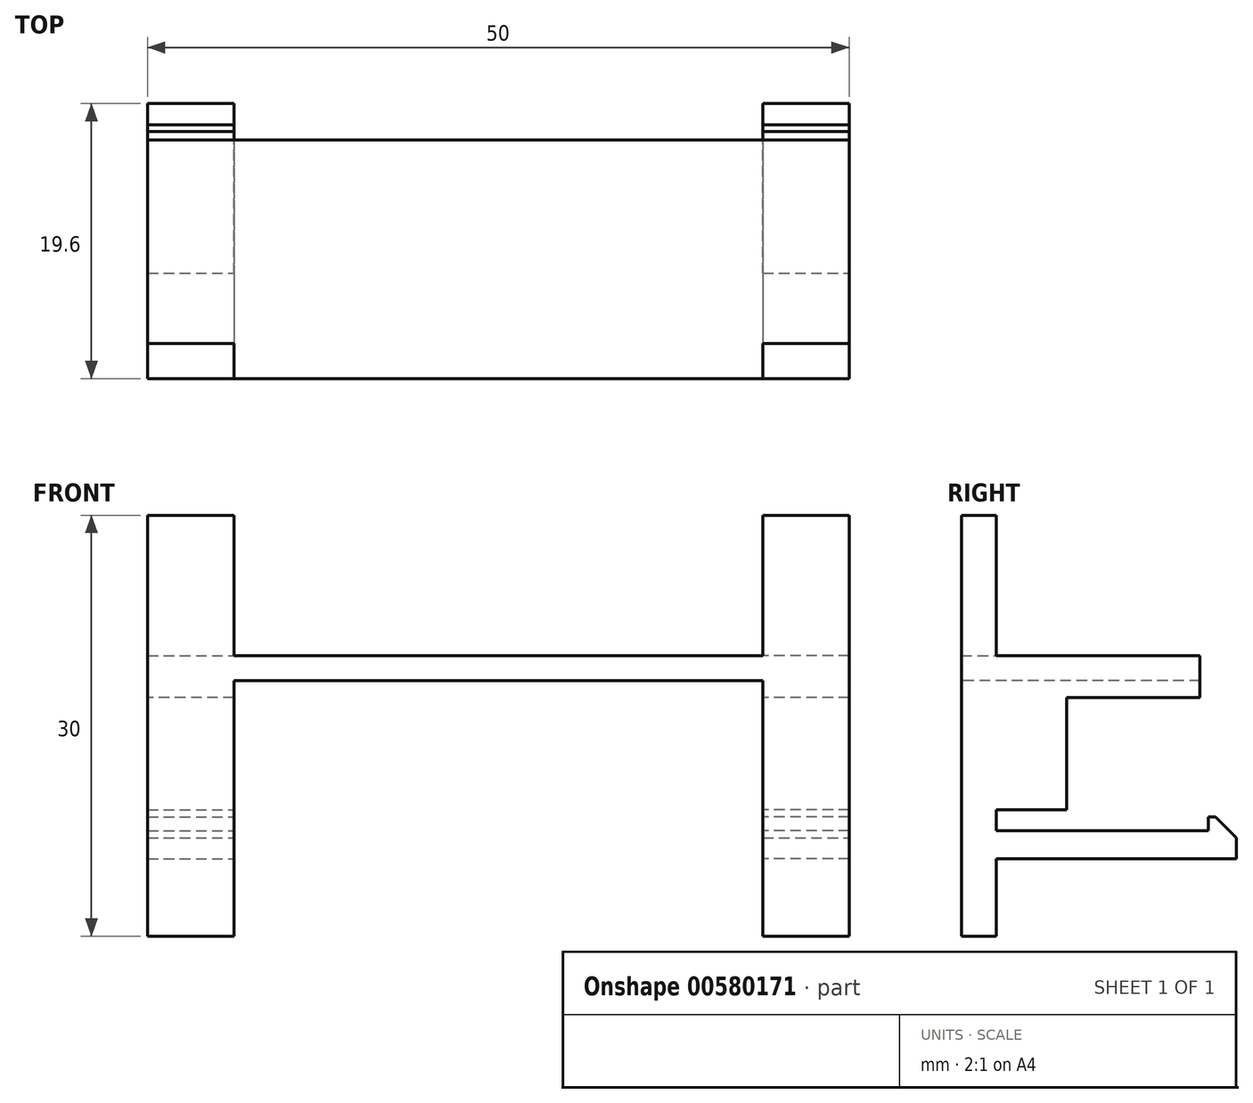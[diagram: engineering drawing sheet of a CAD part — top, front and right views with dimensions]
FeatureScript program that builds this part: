
annotation { "Feature Type Name" : "Feature", "Feature Type Description" : "" }
export const myFeature = defineFeature(function(context is Context, id is Id, definition is map)
    precondition{}
    {
        {
            var Q0;
            Q0=qCreatedBy(makeId("Top.planeOp"),FACE);
            var sketch = newSketch(context, id + "F0", { "sketchPlane" : qUnion([Q0])});
            skLineSegment(sketch, "E0.bottom", {"start": v(25, 8.5) * mm, "end": v(-25, 8.5) * mm});
            skLineSegment(sketch, "E0.top", {"start": v(25, -8.5) * mm, "end": v(-25, -8.5) * mm});
            skLineSegment(sketch, "E0.left", {"start": v(25, 8.5) * mm, "end": v(25, -8.5) * mm});
            skLineSegment(sketch, "E0.right", {"start": v(-25, 8.5) * mm, "end": v(-25, -8.5) * mm});
            skPoint(sketch, "E0.middle", {"position": v(0, 0) * mm});
            skSolve(sketch);
        }
        {
            var Q0;
            Q0=makeQuery(id+"F0.imprint","IMPRINT",FACE,{"disambiguationData":[TD([[makeQuery(id+"F0.imprint","IMPRINT",EDGE,{"derivedFrom":sQuery(id+"F0.wireOp",EDGE,"E0.bottom")}),1.0]])]});
            extrude(context, id + "F1", {"entities" : qUnion([Q0]), "depth" : 11 * mm, "offsetDistance" : 25 * mm});
        }
        {
            var Q0;
            Q0=qCreatedBy(makeId("Front.planeOp"),FACE);
            var sketch = newSketch(context, id + "F2", { "sketchPlane" : qUnion([Q0])});
            skLineSegment(sketch, "E1.bottom", {"start": v(-18.85, 9.2) * mm, "end": v(18.85, 9.2) * mm});
            skLineSegment(sketch, "E1.top", {"start": v(-18.85, -9.2) * mm, "end": v(18.85, -9.2) * mm});
            skLineSegment(sketch, "E1.left", {"start": v(-18.85, 9.2) * mm, "end": v(-18.85, -9.2) * mm});
            skLineSegment(sketch, "E1.right", {"start": v(18.85, 9.2) * mm, "end": v(18.85, -9.2) * mm});
            skPoint(sketch, "E1.middle", {"position": v(0, 0) * mm});
            skSolve(sketch);
        }
        {
            var Q0;
            Q0=makeQuery(id+"F2.imprint","IMPRINT",FACE,{"disambiguationData":[TD([[makeQuery(id+"F2.imprint","IMPRINT",EDGE,{"derivedFrom":sQuery(id+"F2.wireOp",EDGE,"E1.bottom")}),-1.0]])]});
            extrude(context, id + "F3", {"entities" : qUnion([Q0]), "operationType" : NewBodyOperationType.REMOVE, "endBound" : BoundingType.SYMMETRIC, "oppositeDirection" : true, "depth" : 25 * mm, "offsetDistance" : 25 * mm});
        }
        {
            var Q0;
            Q0=makeQuery(id+"F1.opExtrude","SWEPT_FACE",FACE,{"disambiguationData":[OSD([sQuery(id+"F0.wireOp",EDGE,"E0.left")])]});
            var sketch = newSketch(context, id + "F4", { "sketchPlane" : qUnion([Q0])});
            skLineSegment(sketch, "E2", {"start": v(0, 0) * mm, "end": v(0, 11) * mm, "construction": true});
            skArc(sketch, "E3", {"start": v(1, 4) * mm, "mid": v(0, 5) * mm, "end": v(-1, 4) * mm});
            skLineSegment(sketch, "E4.top", {"start": v(1, 0) * mm, "end": v(-1, 0) * mm});
            skLineSegment(sketch, "E4.left", {"start": v(1, 4) * mm, "end": v(1, 0) * mm});
            skLineSegment(sketch, "E4.right", {"start": v(-1, 4) * mm, "end": v(-1, 0) * mm});
            skSolve(sketch);
        }
        {
            var Q0;
            Q0 = qSketchRegion(id + "F4", true);
            extrude(context, id + "F5", {"entities" : qUnion([Q0]), "operationType" : NewBodyOperationType.REMOVE, "endBound" : BoundingType.THROUGH_ALL, "oppositeDirection" : true, "depth" : 25 * mm, "offsetDistance" : 25 * mm});
        }
        {
            var Q0;
            Q0=makeQuery(id+"F1.opExtrude","CAP_FACE",FACE,{"disambiguationData":[OSD([sQuery(id+"F0.wireOp",EDGE,"E0.bottom"),sQuery(id+"F0.wireOp",EDGE,"E0.top"),sQuery(id+"F0.wireOp",EDGE,"E0.left"),sQuery(id+"F0.wireOp",EDGE,"E0.right")])],"isStart":false});
            var sketch = newSketch(context, id + "F6", { "sketchPlane" : qUnion([Q0])});
            skLineSegment(sketch, "E5.bottom", {"start": v(-25, -8.5) * mm, "end": v(-18.85, -8.5) * mm});
            skLineSegment(sketch, "E5.top", {"start": v(-25, -6) * mm, "end": v(-18.85, -6) * mm});
            skLineSegment(sketch, "E5.left", {"start": v(-25, -8.5) * mm, "end": v(-25, -6) * mm});
            skLineSegment(sketch, "E5.right", {"start": v(-18.85, -8.5) * mm, "end": v(-18.85, -6) * mm});
            skLineSegment(sketch, "E6.bottom", {"start": v(25, -8.5) * mm, "end": v(18.85, -8.5) * mm});
            skLineSegment(sketch, "E6.top", {"start": v(25, -6) * mm, "end": v(18.85, -6) * mm});
            skLineSegment(sketch, "E6.left", {"start": v(25, -8.5) * mm, "end": v(25, -6) * mm});
            skLineSegment(sketch, "E6.right", {"start": v(18.85, -8.5) * mm, "end": v(18.85, -6) * mm});
            skSolve(sketch);
        }
        {
            var Q0;
            Q0 = qSketchRegion(id + "F6", true);
            extrude(context, id + "F7", {"entities" : qUnion([Q0]), "operationType" : NewBodyOperationType.ADD, "depth" : 10 * mm, "offsetDistance" : 25 * mm});
        }
        {
            var Q0;
            Q0 = qSketchRegion(id + "F6", true);
            extrude(context, id + "F8", {"entities" : qUnion([Q0]), "operationType" : NewBodyOperationType.ADD, "oppositeDirection" : true, "depth" : 20 * mm, "offsetDistance" : 25 * mm});
        }
        {
            var Q0;
            Q0=makeQuery(id+"F8.opExtrude","SWEPT_FACE",FACE,{"disambiguationData":[OSD([sQuery(id+"F6.wireOp",EDGE,"E6.top")])]});
            var sketch = newSketch(context, id + "F9", { "sketchPlane" : qUnion([Q0])});
            skLineSegment(sketch, "E7.bottom", {"start": v(-25, -1.5) * mm, "end": v(-18.85, -1.5) * mm});
            skLineSegment(sketch, "E7.top", {"start": v(-25, -3.5) * mm, "end": v(-18.85, -3.5) * mm});
            skLineSegment(sketch, "E7.left", {"start": v(-25, -1.5) * mm, "end": v(-25, -3.5) * mm});
            skLineSegment(sketch, "E7.right", {"start": v(-18.85, -1.5) * mm, "end": v(-18.85, -3.5) * mm});
            skLineSegment(sketch, "E8", {"start": v(0, 0.72) * mm, "end": v(0, 16.06) * mm, "construction": true});
            skLineSegment(sketch, "E9.MirrorCS", {"start": v(25, -1.5) * mm, "end": v(25, -3.5) * mm});
            skLineSegment(sketch, "E10.MirrorCS", {"start": v(25, -3.5) * mm, "end": v(18.85, -3.5) * mm});
            skLineSegment(sketch, "E11.MirrorCS", {"start": v(18.85, -1.5) * mm, "end": v(18.85, -3.5) * mm});
            skLineSegment(sketch, "E12.MirrorCS", {"start": v(25, -1.5) * mm, "end": v(18.85, -1.5) * mm});
            skSolve(sketch);
        }
        {
            var Q0;
            Q0 = qSketchRegion(id + "F9", true);
            extrude(context, id + "F10", {"entities" : qUnion([Q0]), "operationType" : NewBodyOperationType.ADD, "depth" : 15.1 * mm, "offsetDistance" : 25 * mm});
        }
        {
            var Q0;
            {var subQ0=sQuery(id+"F6.wireOp",EDGE,"E5.left");Q0=makeQuery(id+"F10.boolean.opBoolean","MERGE",FACE,{"derivedFrom":[makeQuery(id+"F8.boolean.opBoolean","MERGE",FACE,{"derivedFrom":[makeQuery(id+"F7.boolean.opBoolean","MERGE",FACE,{"derivedFrom":[makeQuery(id+"F1.opExtrude","SWEPT_FACE",FACE,{"disambiguationData":[OSD([sQuery(id+"F0.wireOp",EDGE,"E0.right")])]}),makeQuery(id+"F7.opExtrude","SWEPT_FACE",FACE,{"disambiguationData":[OSD([subQ0])]})]}),makeQuery(id+"F8.opExtrude","SWEPT_FACE",FACE,{"disambiguationData":[OSD([subQ0])]})]}),makeQuery(id+"F10.opExtrude","SWEPT_FACE",FACE,{"disambiguationData":[OSD([sQuery(id+"F9.wireOp",EDGE,"E9.MirrorCS")])]})]});}
            var sketch = newSketch(context, id + "F11", { "sketchPlane" : qUnion([Q0])});
            skLineSegment(sketch, "E13.bottom", {"start": v(1, 0) * mm, "end": v(-8.5, 0) * mm});
            skLineSegment(sketch, "E13.top", {"start": v(1, 8) * mm, "end": v(-8.5, 8) * mm});
            skLineSegment(sketch, "E13.left", {"start": v(1, 0) * mm, "end": v(1, 8) * mm});
            skLineSegment(sketch, "E13.right", {"start": v(-8.5, 0) * mm, "end": v(-8.5, 8) * mm});
            skSolve(sketch);
        }
        {
            var Q0;
            Q0 = qSketchRegion(id + "F11", true);
            extrude(context, id + "F12", {"entities" : qUnion([Q0]), "operationType" : NewBodyOperationType.REMOVE, "endBound" : BoundingType.THROUGH_ALL, "oppositeDirection" : true, "depth" : 25 * mm, "offsetDistance" : 25 * mm});
        }
        {
            var Q0;
            Q0=makeQuery(id+"F10.opExtrude","SWEPT_FACE",FACE,{"disambiguationData":[OSD([sQuery(id+"F9.wireOp",EDGE,"E7.top")])]});
            var sketch = newSketch(context, id + "F13", { "sketchPlane" : qUnion([Q0])});
            skLineSegment(sketch, "E14.bottom", {"start": v(25, -9.1) * mm, "end": v(18.85, -9.1) * mm});
            skLineSegment(sketch, "E14.top", {"start": v(25, -11.1) * mm, "end": v(18.85, -11.1) * mm});
            skLineSegment(sketch, "E14.left", {"start": v(25, -9.1) * mm, "end": v(25, -11.1) * mm});
            skLineSegment(sketch, "E14.right", {"start": v(18.85, -9.1) * mm, "end": v(18.85, -11.1) * mm});
            skLineSegment(sketch, "E15.bottom", {"start": v(-25, -9.1) * mm, "end": v(-18.85, -9.1) * mm});
            skLineSegment(sketch, "E15.top", {"start": v(-25, -11.1) * mm, "end": v(-18.85, -11.1) * mm});
            skLineSegment(sketch, "E15.left", {"start": v(-25, -9.1) * mm, "end": v(-25, -11.1) * mm});
            skLineSegment(sketch, "E15.right", {"start": v(-18.85, -9.1) * mm, "end": v(-18.85, -11.1) * mm});
            skSolve(sketch);
        }
        {
            var Q0;
            Q0 = qSketchRegion(id + "F13", true);
            extrude(context, id + "F14", {"entities" : qUnion([Q0]), "operationType" : NewBodyOperationType.ADD, "oppositeDirection" : true, "depth" : 3 * mm, "offsetDistance" : 25 * mm});
        }
        {
            var Q0;
            Q0=makeQuery(id+"F14.opExtrude","CAP_EDGE",EDGE,{"disambiguationData":[OSD([sQuery(id+"F13.wireOp",EDGE,"E14.top")])],"isStart":false});
            var Q1;
            Q1=makeQuery(id+"F14.opExtrude","CAP_EDGE",EDGE,{"disambiguationData":[OSD([sQuery(id+"F13.wireOp",EDGE,"E15.top")])],"isStart":false});
            chamfer(context, id + "F15", {"entities" : qUnion([Q0, Q1]), "width" : 1.5 * mm, "tangentPropagation" : true});
        }
    });
